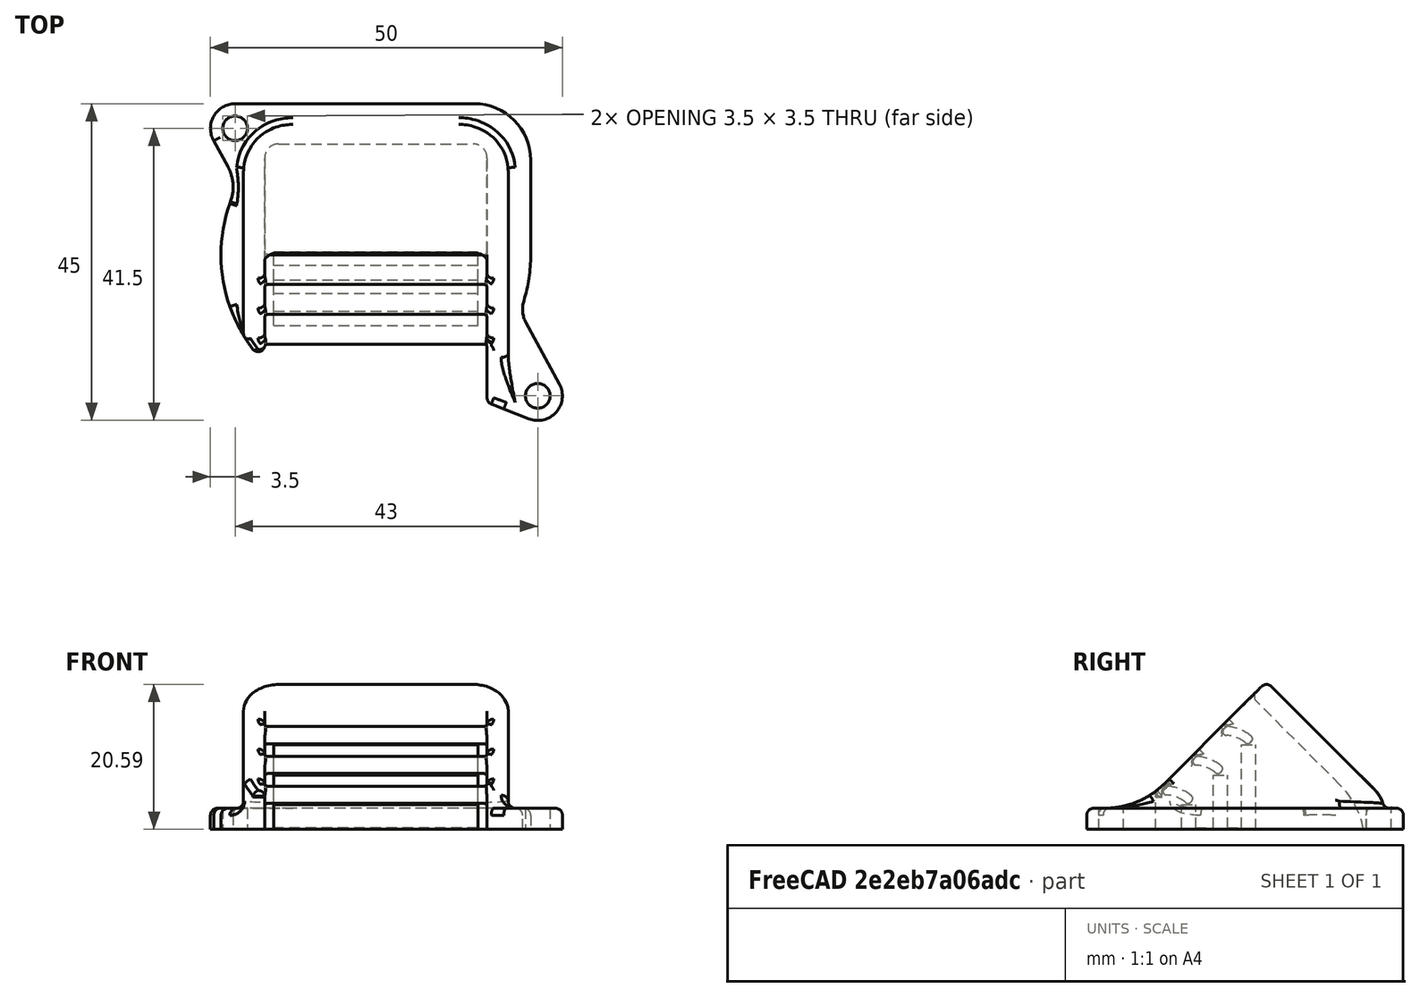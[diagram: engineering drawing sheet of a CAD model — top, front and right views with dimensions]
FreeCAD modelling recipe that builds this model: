
FCSTD DOCUMENT  (FreeCAD 0.18R14555 (Git shallow))
Label: angle-fan-inlet
License: All rights reserved
LicenseURL: http://en.wikipedia.org/wiki/All_rights_reserved
objects: Part::Box×4, Part::Feature×1, Part::MultiFuse×1
note: 6 computed .brp shape members not serialized (recipe doc carries the construction recipe); baked Part::Feature solids carry a one-line shape summary decoded from their .brp

FEATURE [Part::Feature] Part__Feature  label="AIR_INLET_3B"
  shape: bbox 50.32 x 45.69 x 22.35 mm, 185 faces (baked)
FEATURE [Part::Box] Box  label="Cube"
  AttacherType = Attacher::AttachEngine3D
  Height = 12
  Length = 29
  Placement = pos=(-14.5,-1.5,0) rot=(0,0,1;0rad)
  Width = 2
FEATURE [Part::Box] Box001  label="Cube001"
  AttacherType = Attacher::AttachEngine3D
  Height = 7.72
  Length = 29
  Placement = pos=(-14.5,-5.5,0) rot=(0,0,1;0rad)
  Width = 2
FEATURE [Part::Box] Box002  label="Cube002"
  AttacherType = Attacher::AttachEngine3D
  Height = 3.5
  Length = 29
  Placement = pos=(-14.5,-10,0) rot=(0,0,1;0rad)
  Width = 2
FEATURE [Part::Box] Box003  label="Cube003"
  AttacherType = Attacher::AttachEngine3D
  Height = 0.2
  Length = 29
  Placement = pos=(-14.5,-10,0) rot=(0,0,1;0rad)
  Width = 10
FEATURE [Part::MultiFuse] Fusion
  Shapes = -> [Box003,Box,Box002,Box001]
